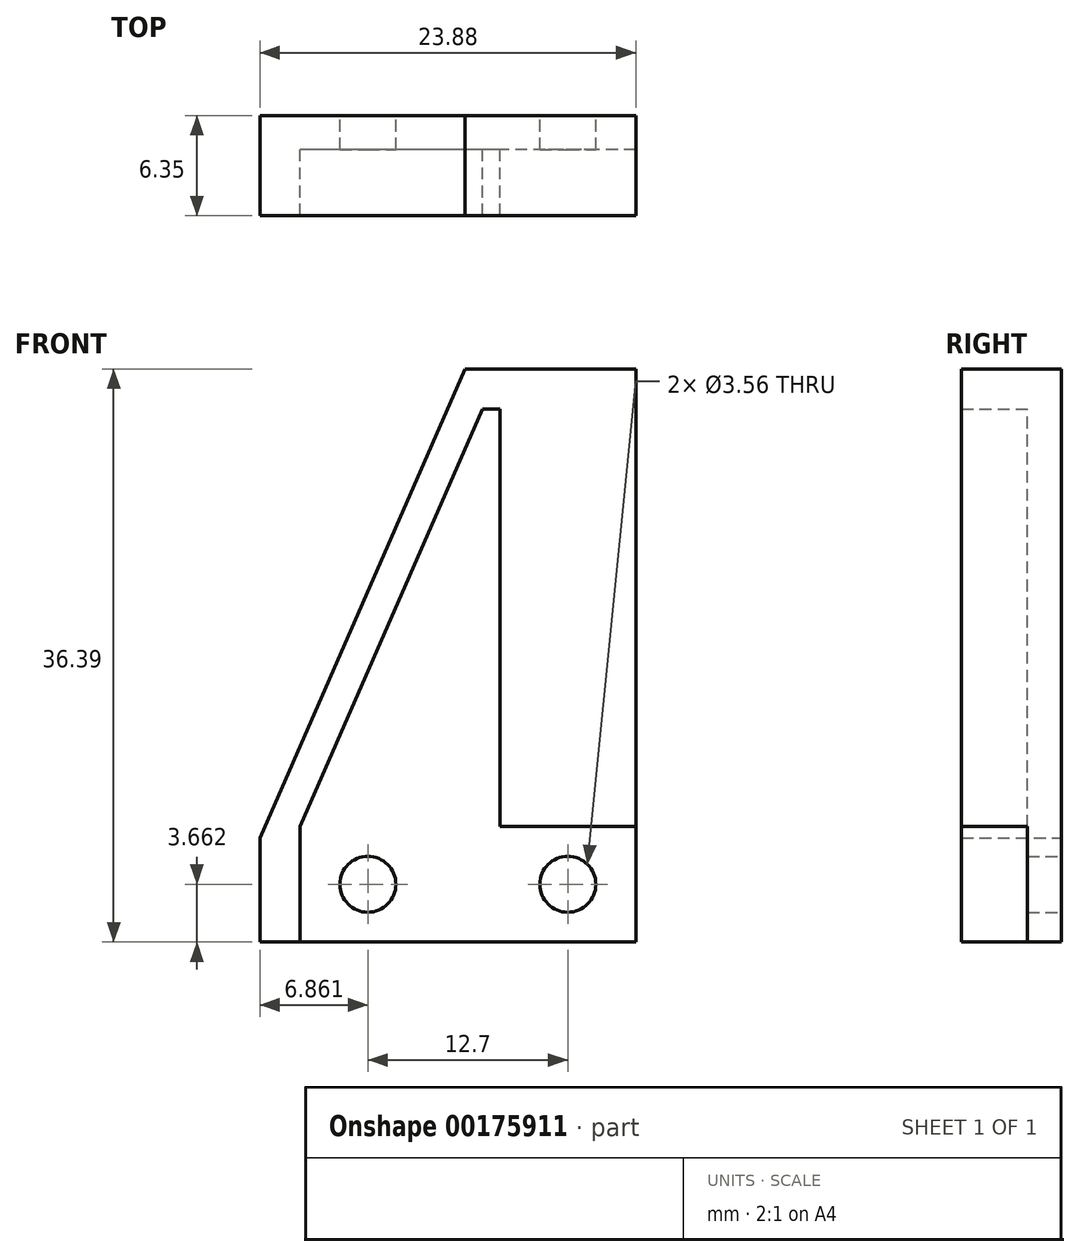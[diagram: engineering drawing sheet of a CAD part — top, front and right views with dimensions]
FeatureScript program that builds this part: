
annotation { "Feature Type Name" : "Feature", "Feature Type Description" : "" }
export const myFeature = defineFeature(function(context is Context, id is Id, definition is map)
    precondition{}
    {
        {
            var Q0;
            Q0=qCreatedBy(makeId("Front.planeOp"),FACE);
            var sketch = newSketch(context, id + "F0", { "sketchPlane" : qUnion([Q0])});
            skLineSegment(sketch, "E0.bottom", {"start": v(-13.9, -13.8) * mm, "end": v(7.43, -13.8) * mm});
            skLineSegment(sketch, "E0.top", {"start": v(-1.2, 22.6) * mm, "end": v(7.43, 22.6) * mm});
            skLineSegment(sketch, "E0.right", {"start": v(7.43, -13.8) * mm, "end": v(7.43, 22.6) * mm});
            skLineSegment(sketch, "E1", {"start": v(-13.9, -13.8) * mm, "end": v(-13.9, -6.46) * mm});
            skCircle(sketch, "E2", {"center": v(-9.59, -10.13) * mm, "radius": 1.78 * mm});
            skPoint(sketch, "E2.centerSnap0", {"position": v(-13.9, -10.13) * mm});
            skCircle(sketch, "E3", {"center": v(3.11, -10.13) * mm, "radius": 1.78 * mm});
            skCircle(sketch, "E4", {"center": v(3.11, 16.25) * mm, "radius": 1.78 * mm, "construction": true});
            skPoint(sketch, "E4.centerSnap0", {"position": v(3.11, 22.6) * mm});
            skCircle(sketch, "E5", {"center": v(3.11, 3.55) * mm, "radius": 1.78 * mm, "construction": true});
            skLineSegment(sketch, "E6", {"start": v(-13.9, -6.46) * mm, "end": v(-2.32, 20.06) * mm});
            skLineSegment(sketch, "E7", {"start": v(-3.43, 22.6) * mm, "end": v(-13.9, -1.38) * mm});
            skLineSegment(sketch, "E8", {"start": v(-3.43, 22.6) * mm, "end": v(-1.2, 22.6) * mm});
            skLineSegment(sketch, "E9", {"start": v(-13.9, -13.8) * mm, "end": v(-16.45, -13.8) * mm});
            skLineSegment(sketch, "E10", {"start": v(-13.9, -1.38) * mm, "end": v(-16.45, -7.2) * mm});
            skLineSegment(sketch, "E11", {"start": v(-16.45, -13.8) * mm, "end": v(-16.45, -7.2) * mm});
            skLineSegment(sketch, "E12", {"start": v(-13.9, -6.46) * mm, "end": v(7.43, -6.46) * mm});
            skLineSegment(sketch, "E13", {"start": v(-13.9, -6.46) * mm, "end": v(-16.13, -6.46) * mm});
            skLineSegment(sketch, "E14.bottom", {"start": v(7.43, 22.6) * mm, "end": v(-1.2, 22.6) * mm});
            skLineSegment(sketch, "E14.top", {"start": v(7.43, -6.46) * mm, "end": v(-1.2, -6.46) * mm});
            skLineSegment(sketch, "E14.left", {"start": v(7.43, 22.6) * mm, "end": v(7.43, -6.46) * mm});
            skLineSegment(sketch, "E14.right", {"start": v(-1.2, 20.06) * mm, "end": v(-1.2, -6.46) * mm});
            skLineSegment(sketch, "E15", {"start": v(-2.32, 20.06) * mm, "end": v(-1.2, 20.06) * mm});
            skSolve(sketch);
        }
        {
            var Q0;
            Q0 = qSketchRegion(id + "F0", true);
            var Q1;
            Q1=makeQuery(id+"F0.imprint","IMPRINT",FACE,{"disambiguationData":[TD([[makeQuery(id+"F0.imprint","IMPRINT",EDGE,{"derivedFrom":sQuery(id+"F0.wireOp",EDGE,"E6")}),-1.0]])]});
            extrude(context, id + "F1", {"entities" : qUnion([Q0, Q1]), "depth" : 2.16 * mm});
        }
        {
            var Q0;
            Q0=makeQuery(id+"F0.imprint","IMPRINT",FACE,{"disambiguationData":[TD([[makeQuery(id+"F0.imprint","IMPRINT",EDGE,{"derivedFrom":sQuery(id+"F0.wireOp",EDGE,"E6")}),1.0]])]});
            var Q1;
            Q1=makeQuery(id+"F0.imprint","IMPRINT",FACE,{"disambiguationData":[TD([[makeQuery(id+"F0.imprint","IMPRINT",EDGE,{"derivedFrom":sQuery(id+"F0.wireOp",EDGE,"E1")}),1.0]])]});
            var Q2;
            Q2=makeQuery(id+"F0.imprint","IMPRINT",FACE,{"disambiguationData":[TD([[makeQuery(id+"F0.imprint","IMPRINT",EDGE,{"derivedFrom":sQuery(id+"F0.wireOp",EDGE,"E4")}),-1.0]])]});
            extrude(context, id + "F2", {"entities" : qUnion([Q0, Q1, Q2]), "operationType" : NewBodyOperationType.ADD, "depth" : 6.35 * mm});
        }
    });
